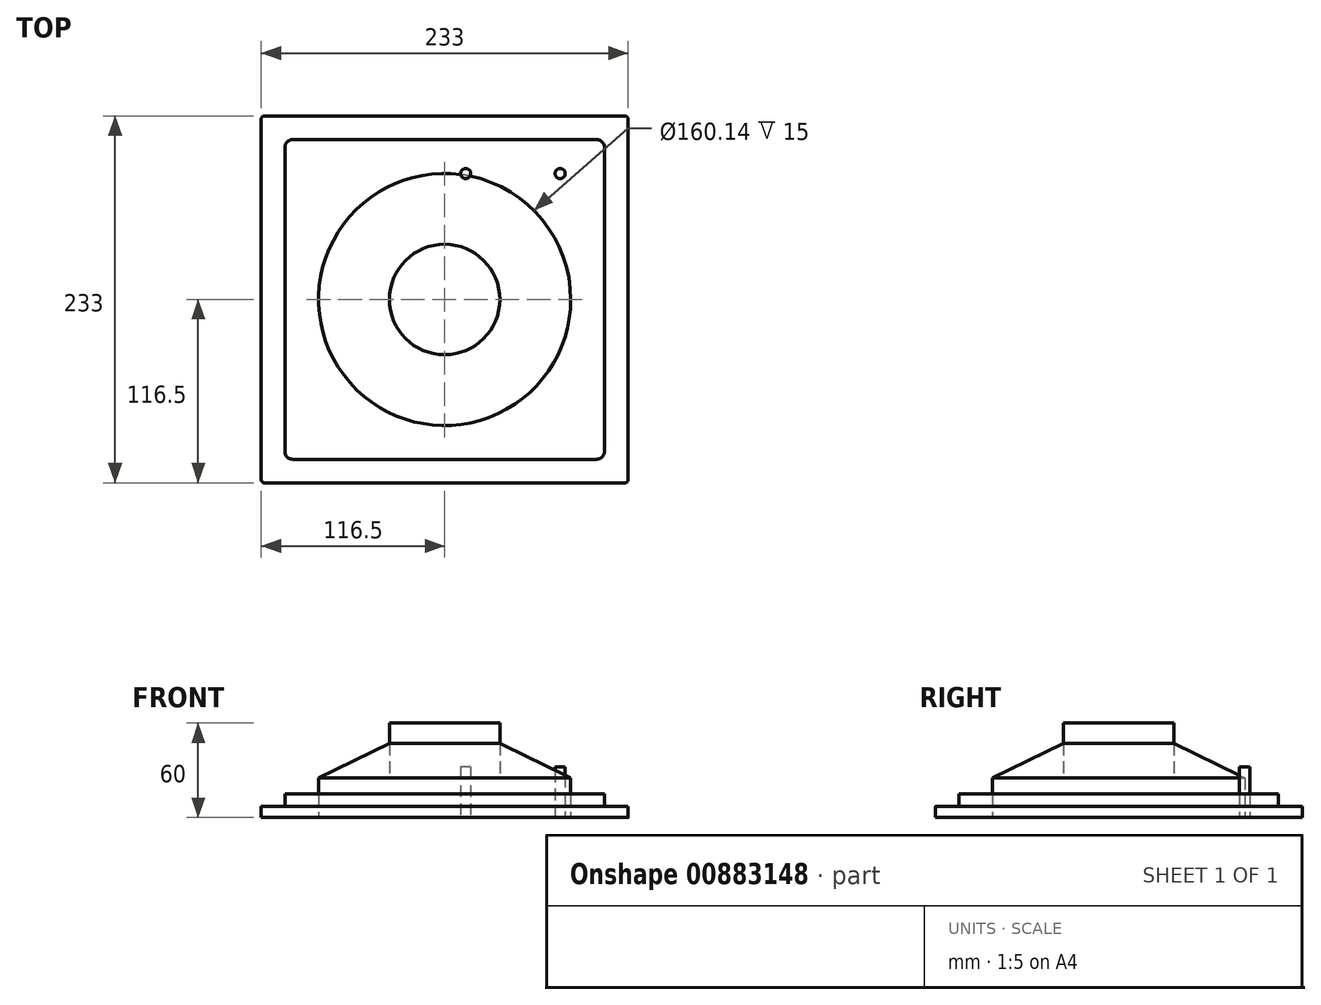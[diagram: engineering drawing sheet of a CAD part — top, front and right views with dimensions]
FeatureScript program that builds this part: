
annotation { "Feature Type Name" : "Feature", "Feature Type Description" : "" }
export const myFeature = defineFeature(function(context is Context, id is Id, definition is map)
    precondition{}
    {
        {
            var Q0;
            Q0=qCreatedBy(makeId("Top.planeOp"),FACE);
            var sketch = newSketch(context, id + "F0", { "sketchPlane" : qUnion([Q0])});
            skLineSegment(sketch, "E0.bottom", {"start": v(-114.5, 116.5) * mm, "end": v(114.5, 116.5) * mm});
            skLineSegment(sketch, "E0.top", {"start": v(-114.5, -116.5) * mm, "end": v(114.5, -116.5) * mm});
            skLineSegment(sketch, "E0.left", {"start": v(-116.5, 114.5) * mm, "end": v(-116.5, -114.5) * mm});
            skLineSegment(sketch, "E0.right", {"start": v(116.5, 114.5) * mm, "end": v(116.5, -114.5) * mm});
            skLineSegment(sketch, "E1.0", {"start": v(-101.5, 96.5) * mm, "end": v(-101.5, -96.5) * mm});
            skLineSegment(sketch, "E2.0", {"start": v(-96.5, 101.5) * mm, "end": v(96.5, 101.5) * mm});
            skLineSegment(sketch, "E3.0", {"start": v(101.5, 96.5) * mm, "end": v(101.5, -96.5) * mm});
            skLineSegment(sketch, "E4.0", {"start": v(-96.5, -101.5) * mm, "end": v(96.5, -101.5) * mm});
            skLineSegment(sketch, "E5", {"start": v(-101.5, 101.5) * mm, "end": v(101.5, -101.5) * mm, "construction": true});
            skLineSegment(sketch, "E6", {"start": v(-101.5, -101.5) * mm, "end": v(101.5, 101.5) * mm, "construction": true});
            skCircle(sketch, "E7", {"center": v(0, 0) * mm, "radius": 80.07 * mm});
            skCircle(sketch, "E8", {"center": v(0, 0) * mm, "radius": 35.09 * mm});
            skPoint(sketch, "E9.visualSharp", {"position": v(101.5, -101.5) * mm});
            skArc(sketch, "E9.filletArc", {"start": v(96.5, -101.5) * mm, "mid": v(100.04, -100.04) * mm, "end": v(101.5, -96.5) * mm});
            skPoint(sketch, "E10.visualSharp", {"position": v(-101.5, -101.5) * mm});
            skArc(sketch, "E10.filletArc", {"start": v(-101.5, -96.5) * mm, "mid": v(-100.04, -100.04) * mm, "end": v(-96.5, -101.5) * mm});
            skPoint(sketch, "E11.visualSharp", {"position": v(-101.5, 101.5) * mm});
            skArc(sketch, "E11.filletArc", {"start": v(-96.5, 101.5) * mm, "mid": v(-100.04, 100.04) * mm, "end": v(-101.5, 96.5) * mm});
            skPoint(sketch, "E12.visualSharp", {"position": v(101.5, 101.5) * mm});
            skArc(sketch, "E12.filletArc", {"start": v(101.5, 96.5) * mm, "mid": v(100.04, 100.04) * mm, "end": v(96.5, 101.5) * mm});
            skPoint(sketch, "E13.visualSharp", {"position": v(-116.5, -116.5) * mm});
            skArc(sketch, "E13.filletArc", {"start": v(-116.5, -114.5) * mm, "mid": v(-115.91, -115.91) * mm, "end": v(-114.5, -116.5) * mm});
            skPoint(sketch, "E14.visualSharp", {"position": v(116.5, -116.5) * mm});
            skArc(sketch, "E14.filletArc", {"start": v(114.5, -116.5) * mm, "mid": v(115.91, -115.91) * mm, "end": v(116.5, -114.5) * mm});
            skPoint(sketch, "E15.visualSharp", {"position": v(116.5, 116.5) * mm});
            skArc(sketch, "E15.filletArc", {"start": v(116.5, 114.5) * mm, "mid": v(115.91, 115.91) * mm, "end": v(114.5, 116.5) * mm});
            skPoint(sketch, "E16.visualSharp", {"position": v(-116.5, 116.5) * mm});
            skArc(sketch, "E16.filletArc", {"start": v(-114.5, 116.5) * mm, "mid": v(-115.91, 115.91) * mm, "end": v(-116.5, 114.5) * mm});
            skSolve(sketch);
        }
        {
            var Q0;
            Q0=makeQuery(id+"F0.imprint","IMPRINT",FACE,{"disambiguationData":[TD([[makeQuery(id+"F0.imprint","IMPRINT",EDGE,{"derivedFrom":sQuery(id+"F0.wireOp",EDGE,"E1.0")}),1.0]])]});
            extrude(context, id + "F1", {"entities" : qUnion([Q0]), "depth" : 15 * mm, "offsetDistance" : 25 * mm});
        }
        {
            var Q0;
            Q0 = qSketchRegion(id + "F0", true);
            extrude(context, id + "F2", {"entities" : qUnion([Q0]), "operationType" : NewBodyOperationType.ADD, "depth" : 7 * mm, "offsetDistance" : 25 * mm});
        }
        {
            var Q0;
            Q0=makeQuery(id+"F1.opExtrude","CAP_FACE",FACE,{"disambiguationData":[OSD([sQuery(id+"F0.wireOp",EDGE,"E1.0"),sQuery(id+"F0.wireOp",EDGE,"E2.0"),sQuery(id+"F0.wireOp",EDGE,"E3.0"),sQuery(id+"F0.wireOp",EDGE,"E4.0")])],"isStart":false});
            var sketch = newSketch(context, id + "F3", { "sketchPlane" : qUnion([Q0])});
            skLineSegment(sketch, "E17", {"start": v(86.7, -101.5) * mm, "end": v(86.7, -86.7) * mm, "construction": true});
            skLineSegment(sketch, "E18", {"start": v(86.7, -86.7) * mm, "end": v(101.5, -86.7) * mm, "construction": true});
            skCircle(sketch, "E19", {"center": v(86.7, -86.7) * mm, "radius": 4.86 * mm});
            skCircle(sketch, "E20.MirrorC", {"center": v(-86.7, -86.7) * mm, "radius": 4.86 * mm});
            skCircle(sketch, "E21.MirrorC", {"center": v(-86.7, 86.7) * mm, "radius": 4.86 * mm});
            skCircle(sketch, "E22.MirrorC", {"center": v(86.7, 86.7) * mm, "radius": 4.86 * mm});
            skSolve(sketch);
        }
        {
            var Q0;
            Q0=makeQuery(id+"F3.imprint","IMPRINT",FACE,{"disambiguationData":[TD([[makeQuery(id+"F3.imprint","IMPRINT",EDGE,{"derivedFrom":sQuery(id+"F3.wireOp",EDGE,"E21.MirrorC")}),1.0]])]});
            var sketch = newSketch(context, id + "F4", { "sketchPlane" : qUnion([Q0])});
            skCircle(sketch, "E23", {"center": v(86.74, -86.7) * mm, "radius": 9.8 * mm});
            skCircle(sketch, "E24.MirrorC", {"center": v(-86.74, -86.7) * mm, "radius": 9.8 * mm});
            skCircle(sketch, "E25.MirrorC", {"center": v(-86.74, 86.7) * mm, "radius": 9.8 * mm});
            skCircle(sketch, "E26.MirrorC", {"center": v(86.74, 86.7) * mm, "radius": 9.8 * mm});
            skSolve(sketch);
        }
        {
            var Q0;
            Q0=sQuery(id+"F4.wireOp",EDGE,"E25.MirrorC");
            var Q1;
            Q1=sQuery(id+"F3.wireOp",EDGE,"E21.MirrorC");
            var Q2;
            Q2=sQuery(id+"F4.wireOp",EDGE,"E24.MirrorC");
            var Q3;
            Q3=sQuery(id+"F3.wireOp",EDGE,"E20.MirrorC");
            var Q4;
            Q4=sQuery(id+"F3.wireOp",EDGE,"E19");
            var Q5;
            Q5=sQuery(id+"F4.wireOp",EDGE,"E23");
            var Q6;
            Q6=sQuery(id+"F4.wireOp",EDGE,"E26.MirrorC");
            var Q7;
            Q7=sQuery(id+"F3.wireOp",EDGE,"E22.MirrorC");
            extrude(context, id + "F5", {"bodyType" : ToolBodyType.SURFACE, "surfaceEntities" : qUnion([Q0, Q1, Q2, Q3, Q4, Q5, Q6, Q7]), "depth" : 54.5 * mm, "offsetDistance" : 25 * mm});
        }
        {
            var Q0;
            Q0=qCreatedBy(makeId("Top.planeOp"),FACE);
            var sketch = newSketch(context, id + "F6", { "sketchPlane" : qUnion([Q0])});
            skLineSegment(sketch, "E27", {"start": v(117.38, 80) * mm, "end": v(73.38, 80) * mm, "construction": true});
            skLineSegment(sketch, "E28", {"start": v(73.38, 80) * mm, "end": v(73.38, 117) * mm, "construction": true});
            skLineSegment(sketch, "E29", {"start": v(73.38, 116.55) * mm, "end": v(73.38, 117) * mm});
            skLineSegment(sketch, "E30", {"start": v(73.38, 80) * mm, "end": v(13.38, 80) * mm, "construction": true});
            skCircle(sketch, "E31", {"center": v(13.38, 80) * mm, "radius": 3.21 * mm});
            skCircle(sketch, "E32", {"center": v(73.38, 80) * mm, "radius": 3.22 * mm});
            skSolve(sketch);
        }
        {
            var Q0;
            Q0=makeQuery(id+"F0.imprint","IMPRINT",FACE,{"disambiguationData":[TD([[makeQuery(id+"F0.imprint","IMPRINT",EDGE,{"derivedFrom":sQuery(id+"F0.wireOp",EDGE,"E8")}),1.0]])]});
            extrude(context, id + "F7", {"entities" : qUnion([Q0]), "depth" : 47 * mm, "offsetDistance" : 25 * mm, "hasSecondDirection" : true, "secondDirectionOppositeDirection" : true, "secondDirectionDepth" : -25 * mm});
        }
        {
            var Q0;
            Q0=makeQuery(id+"F0.imprint","IMPRINT",FACE,{"disambiguationData":[TD([[makeQuery(id+"F0.imprint","IMPRINT",EDGE,{"derivedFrom":sQuery(id+"F0.wireOp",EDGE,"E7")}),1.0]])]});
            var Q1;
            Q1=makeQuery(id+"F0.imprint","IMPRINT",FACE,{"disambiguationData":[TD([[makeQuery(id+"F0.imprint","IMPRINT",EDGE,{"derivedFrom":sQuery(id+"F0.wireOp",EDGE,"E8")}),1.0]])]});
            extrude(context, id + "F8", {"entities" : qUnion([Q0, Q1]), "depth" : 25 * mm, "offsetDistance" : 25 * mm});
        }
        {
            var Q0;
            Q0=makeQuery(id+"F8.opExtrude","CAP_FACE",FACE,{"disambiguationData":[OSD([sQuery(id+"F0.wireOp",EDGE,"E7")])],"isStart":false});
            var Q1;
            Q1=makeQuery(id+"F7.opExtrude","CAP_FACE",FACE,{"disambiguationData":[OSD([sQuery(id+"F0.wireOp",EDGE,"E8")])],"isStart":false});
            loft(context, id + "F9", {"sheetProfilesArray" : [{ "sheetProfileEntities" : qUnion([Q0]) }, { "sheetProfileEntities" : qUnion([Q1]) }]});
        }
        {
            var Q0;
            Q0=makeQuery(id+"F7.opExtrude","CAP_FACE",FACE,{"disambiguationData":[OSD([sQuery(id+"F0.wireOp",EDGE,"E8")])],"isStart":false});
            extrude(context, id + "F10", {"entities" : qUnion([Q0]), "depth" : 13 * mm, "offsetDistance" : 25 * mm});
        }
        {
            var Q0;
            Q0 = qSketchRegion(id + "F6", true);
            extrude(context, id + "F11", {"entities" : qUnion([Q0]), "depth" : 32 * mm, "offsetDistance" : 25 * mm});
        }
    });
